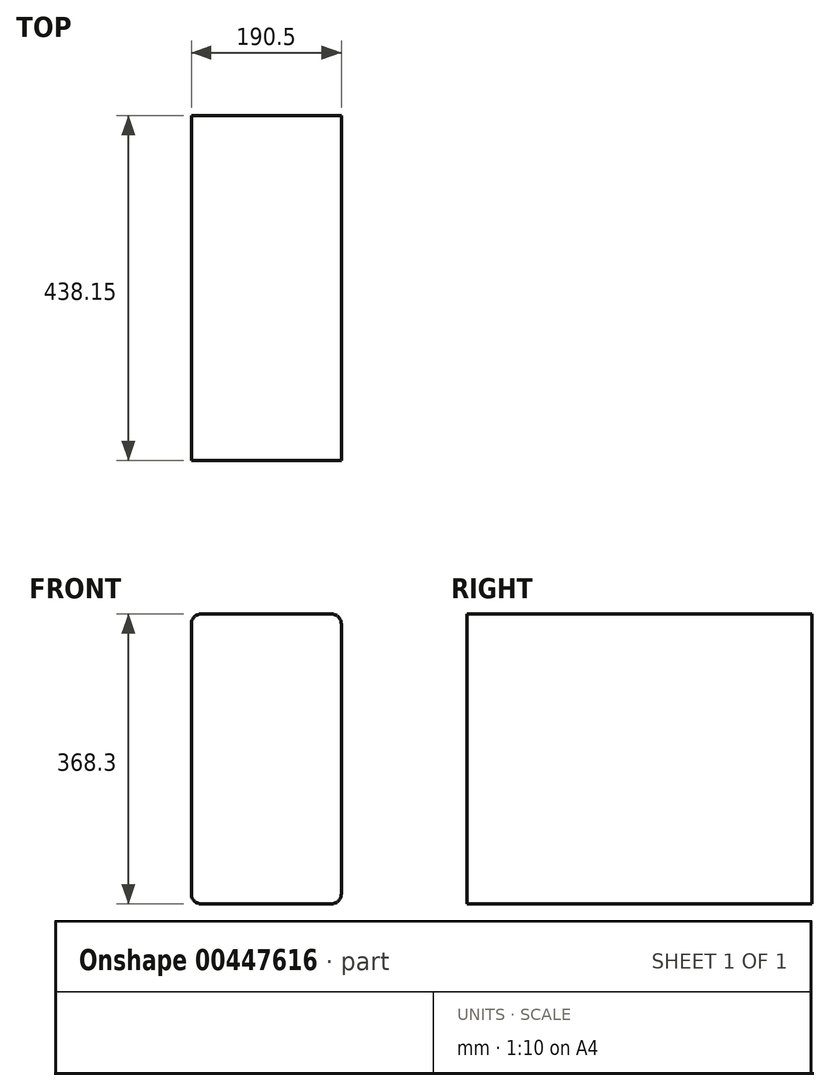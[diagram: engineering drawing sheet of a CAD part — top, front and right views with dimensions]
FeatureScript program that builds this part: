
annotation { "Feature Type Name" : "Feature", "Feature Type Description" : "" }
export const myFeature = defineFeature(function(context is Context, id is Id, definition is map)
    precondition{}
    {
        {
            var Q0;
            Q0=qCreatedBy(makeId("Front.planeOp"),FACE);
            var sketch = newSketch(context, id + "F0", { "sketchPlane" : qUnion([Q0])});
            skLineSegment(sketch, "E0.bottom", {"start": v(0, 0) * mm, "end": v(190.5, 0) * mm});
            skLineSegment(sketch, "E0.top", {"start": v(0, 368.3) * mm, "end": v(190.5, 368.3) * mm});
            skLineSegment(sketch, "E0.left", {"start": v(0, 0) * mm, "end": v(0, 368.3) * mm});
            skLineSegment(sketch, "E0.right", {"start": v(190.5, 0) * mm, "end": v(190.5, 368.3) * mm});
            skSolve(sketch);
        }
        {
            var Q0;
            Q0 = qSketchRegion(id + "F0", true);
            extrude(context, id + "F1", {"entities" : qUnion([Q0]), "oppositeDirection" : true, "depth" : 438.15 * mm});
        }
        {
            var Q0;
            Q0=makeQuery(id+"F1.opExtrude","SWEPT_EDGE",EDGE,{"disambiguationData":[OSD([sQuery(id+"F0.wireOp",EDGE,"E0.top"),sQuery(id+"F0.wireOp",EDGE,"E0.left")])]});
            var Q1;
            Q1=makeQuery(id+"F1.opExtrude","SWEPT_EDGE",EDGE,{"disambiguationData":[OSD([sQuery(id+"F0.wireOp",EDGE,"E0.top"),sQuery(id+"F0.wireOp",EDGE,"E0.right")])]});
            var Q2;
            Q2=makeQuery(id+"F1.opExtrude","SWEPT_EDGE",EDGE,{"disambiguationData":[OSD([sQuery(id+"F0.wireOp",EDGE,"E0.bottom"),sQuery(id+"F0.wireOp",EDGE,"E0.right")])]});
            var Q3;
            Q3=makeQuery(id+"F1.opExtrude","SWEPT_EDGE",EDGE,{"disambiguationData":[OSD([sQuery(id+"F0.wireOp",EDGE,"E0.bottom"),sQuery(id+"F0.wireOp",EDGE,"E0.left")])]});
            fillet(context, id + "F2", {"entities" : qUnion([Q0, Q1, Q2, Q3]), "radius" : 12.7 * mm, "tangentPropagation" : true, "allowEdgeOverflow" : false});
        }
    });
